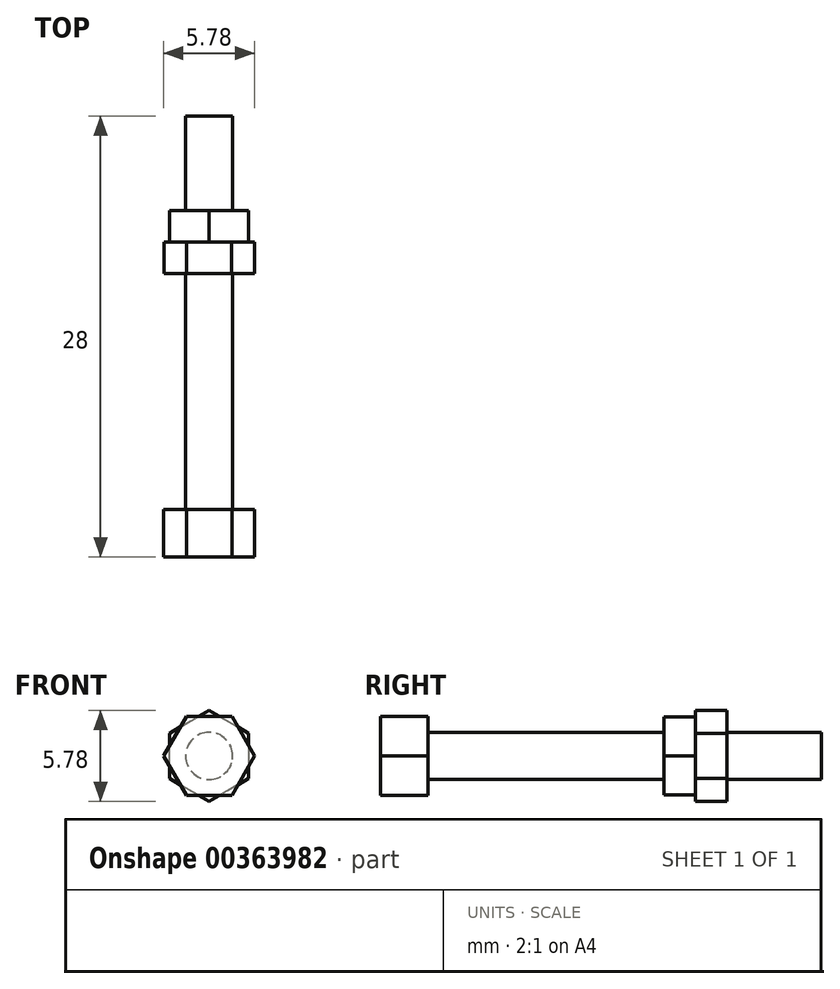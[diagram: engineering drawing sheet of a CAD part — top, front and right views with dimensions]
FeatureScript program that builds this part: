
annotation { "Feature Type Name" : "Feature", "Feature Type Description" : "" }
export const myFeature = defineFeature(function(context is Context, id is Id, definition is map)
    precondition{}
    {
        {
            var Q0;
            Q0=qCreatedBy(makeId("Front.planeOp"),FACE);
            var sketch = newSketch(context, id + "F0", { "sketchPlane" : qUnion([Q0])});
            skCircle(sketch, "E0.cCircle", {"center": v(0, 0) * mm, "radius": 2.5 * mm, "construction": true});
            skLineSegment(sketch, "E0.0", {"start": v(1.44, -2.5) * mm, "end": v(-1.44, -2.5) * mm});
            skLineSegment(sketch, "E0.1", {"start": v(-1.44, -2.5) * mm, "end": v(-2.89, 0) * mm});
            skLineSegment(sketch, "E0.2", {"start": v(-2.89, 0) * mm, "end": v(-1.44, 2.5) * mm});
            skLineSegment(sketch, "E0.3", {"start": v(-1.44, 2.5) * mm, "end": v(1.44, 2.5) * mm});
            skLineSegment(sketch, "E0.4", {"start": v(1.44, 2.5) * mm, "end": v(2.89, 0) * mm});
            skLineSegment(sketch, "E0.5", {"start": v(2.89, 0) * mm, "end": v(1.44, -2.5) * mm});
            skPoint(sketch, "E0.0.midPoint", {"position": v(0, -2.5) * mm});
            skSolve(sketch);
        }
        {
            var Q0;
            Q0=makeQuery(id+"F0.imprint","IMPRINT",FACE,{"disambiguationData":[TD([[makeQuery(id+"F0.imprint","IMPRINT",EDGE,{"derivedFrom":sQuery(id+"F0.wireOp",EDGE,"E0.0")}),-1.0]])]});
            extrude(context, id + "F1", {"entities" : qUnion([Q0]), "depth" : 3 * mm});
        }
        {
            var Q0;
            Q0=makeQuery(id+"F1.opExtrude","CAP_FACE",FACE,{"disambiguationData":[OSD([sQuery(id+"F0.wireOp",EDGE,"E0.0"),sQuery(id+"F0.wireOp",EDGE,"E0.1"),sQuery(id+"F0.wireOp",EDGE,"E0.2"),sQuery(id+"F0.wireOp",EDGE,"E0.3"),sQuery(id+"F0.wireOp",EDGE,"E0.4"),sQuery(id+"F0.wireOp",EDGE,"E0.5")])],"isStart":true});
            var sketch = newSketch(context, id + "F2", { "sketchPlane" : qUnion([Q0])});
            skCircle(sketch, "E1", {"center": v(0, 0) * mm, "radius": 1.5 * mm});
            skSolve(sketch);
        }
        {
            var Q0;
            Q0=makeQuery(id+"F2.imprint","IMPRINT",FACE,{"disambiguationData":[TD([[makeQuery(id+"F2.imprint","IMPRINT",EDGE,{"derivedFrom":sQuery(id+"F2.wireOp",EDGE,"E1")}),1.0]])]});
            extrude(context, id + "F3", {"entities" : qUnion([Q0]), "operationType" : NewBodyOperationType.ADD, "depth" : 25 * mm});
        }
        {
            var Q0;
            Q0=qCreatedBy(makeId("Front.planeOp"),FACE);
            cPlane(context, id + "F4", {"entities" : qUnion([Q0]), "cplaneType" : CPlaneType.OFFSET, "offset" : 15 * mm, "oppositeDirection" : true, "width" : 150 * mm, "height" : 150 * mm});
        }
        {
            var Q0;
            Q0=qCreatedBy(id+"F4.planeOp",FACE);
            var sketch = newSketch(context, id + "F5", { "sketchPlane" : qUnion([Q0])});
            skCircle(sketch, "E2.cCircle", {"center": v(0, 0) * mm, "radius": 2.49 * mm, "construction": true});
            skLineSegment(sketch, "E2.0", {"start": v(-1.44, 2.49) * mm, "end": v(1.44, 2.49) * mm});
            skLineSegment(sketch, "E2.1", {"start": v(1.44, 2.49) * mm, "end": v(2.87, 0) * mm});
            skLineSegment(sketch, "E2.2", {"start": v(2.87, 0) * mm, "end": v(1.44, -2.49) * mm});
            skLineSegment(sketch, "E2.3", {"start": v(1.44, -2.49) * mm, "end": v(-1.44, -2.49) * mm});
            skLineSegment(sketch, "E2.4", {"start": v(-1.44, -2.49) * mm, "end": v(-2.87, 0) * mm});
            skLineSegment(sketch, "E2.5", {"start": v(-2.87, 0) * mm, "end": v(-1.44, 2.49) * mm});
            skPoint(sketch, "E2.0.midPoint", {"position": v(0, 2.49) * mm});
            skSolve(sketch);
        }
        {
            var Q0;
            Q0=makeQuery(id+"F5.imprint","IMPRINT",FACE,{"disambiguationData":[TD([[makeQuery(id+"F5.imprint","IMPRINT",EDGE,{"derivedFrom":sQuery(id+"F5.wireOp",EDGE,"E2.0")}),-1.0]])]});
            extrude(context, id + "F6", {"entities" : qUnion([Q0]), "operationType" : NewBodyOperationType.ADD, "oppositeDirection" : true, "depth" : 2 * mm});
        }
        {
            var Q0;
            Q0=qCreatedBy(id+"F4.planeOp",FACE);
            cPlane(context, id + "F7", {"entities" : qUnion([Q0]), "cplaneType" : CPlaneType.OFFSET, "offset" : 2 * mm, "oppositeDirection" : true, "width" : 150 * mm, "height" : 150 * mm});
        }
        {
            var Q0;
            Q0=qCreatedBy(id+"F7.planeOp",FACE);
            var sketch = newSketch(context, id + "F8", { "sketchPlane" : qUnion([Q0])});
            skCircle(sketch, "E3.cCircle", {"center": v(0, 0) * mm, "radius": 2.5 * mm, "construction": true});
            skLineSegment(sketch, "E3.0", {"start": v(2.5, 1.44) * mm, "end": v(2.5, -1.44) * mm});
            skLineSegment(sketch, "E3.1", {"start": v(2.5, -1.44) * mm, "end": v(0, -2.89) * mm});
            skLineSegment(sketch, "E3.2", {"start": v(0, -2.89) * mm, "end": v(-2.5, -1.44) * mm});
            skLineSegment(sketch, "E3.3", {"start": v(-2.5, -1.44) * mm, "end": v(-2.5, 1.44) * mm});
            skLineSegment(sketch, "E3.4", {"start": v(-2.5, 1.44) * mm, "end": v(0, 2.89) * mm});
            skLineSegment(sketch, "E3.5", {"start": v(0, 2.89) * mm, "end": v(2.5, 1.44) * mm});
            skPoint(sketch, "E3.0.midPoint", {"position": v(2.5, 0) * mm});
            skSolve(sketch);
        }
        {
            var Q0;
            Q0=makeQuery(id+"F8.imprint","IMPRINT",FACE,{"disambiguationData":[TD([[makeQuery(id+"F8.imprint","IMPRINT",EDGE,{"derivedFrom":sQuery(id+"F8.wireOp",EDGE,"E3.0")}),-1.0]])]});
            extrude(context, id + "F9", {"entities" : qUnion([Q0]), "operationType" : NewBodyOperationType.ADD, "oppositeDirection" : true, "depth" : 2 * mm});
        }
    });
